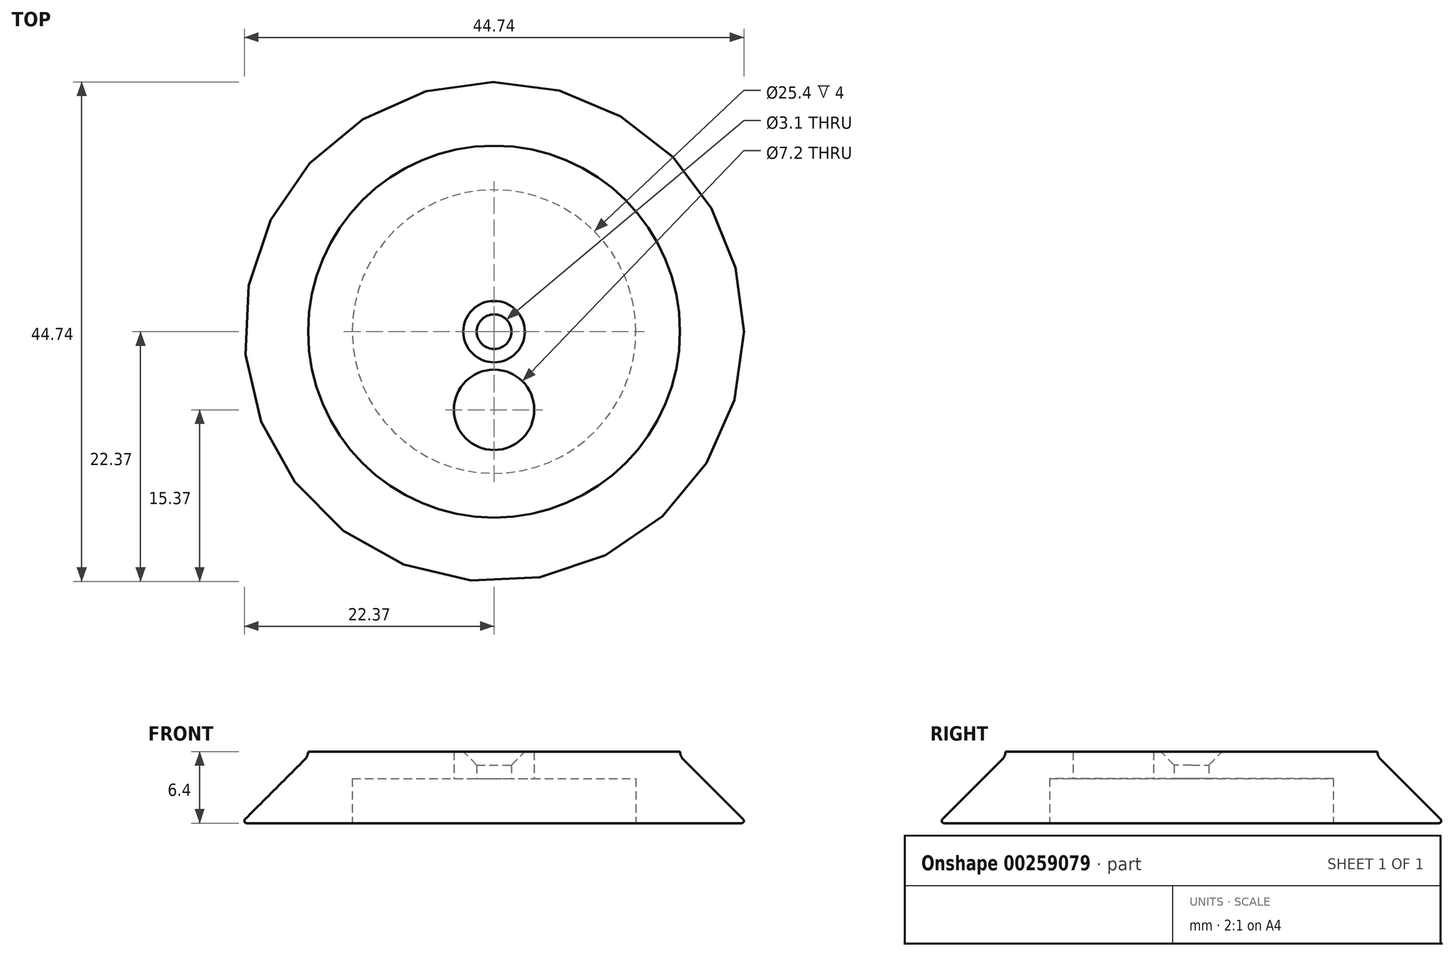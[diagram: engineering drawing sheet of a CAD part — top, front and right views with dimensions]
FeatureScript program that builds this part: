
annotation { "Feature Type Name" : "Feature", "Feature Type Description" : "" }
export const myFeature = defineFeature(function(context is Context, id is Id, definition is map)
    precondition{}
    {
        {
            var Q0;
            Q0=qCreatedBy(makeId("Top.planeOp"),FACE);
            var sketch = newSketch(context, id + "F0", { "sketchPlane" : qUnion([Q0])});
            skCircle(sketch, "E0", {"center": v(0, 0) * mm, "radius": 22.65 * mm});
            skSolve(sketch);
        }
        {
            var Q0;
            Q0 = qSketchRegion(id + "F0", true);
            extrude(context, id + "F1", {"entities" : qUnion([Q0]), "depth" : 6 * mm});
        }
        {
            var Q0;
            Q0=makeQuery(id+"F1.opExtrude","CAP_EDGE",EDGE,{"disambiguationData":[OSD([sQuery(id+"F0.wireOp",EDGE,"E0")])],"isStart":false});
            chamfer(context, id + "F2", {"entities" : qUnion([Q0]), "width" : 6 * mm, "tangentPropagation" : true});
        }
        {
            var Q0;
            Q0=makeQuery(id+"F1.opExtrude","CAP_FACE",FACE,{"disambiguationData":[OSD([sQuery(id+"F0.wireOp",EDGE,"E0")])],"isStart":false});
            extrude(context, id + "F3", {"entities" : qUnion([Q0]), "operationType" : NewBodyOperationType.ADD, "depth" : 0.4 * mm});
        }
        {
            var Q0;
            Q0=makeQuery(id+"F1.opExtrude","CAP_FACE",FACE,{"disambiguationData":[OSD([sQuery(id+"F0.wireOp",EDGE,"E0")])],"isStart":true});
            var sketch = newSketch(context, id + "F4", { "sketchPlane" : qUnion([Q0])});
            skCircle(sketch, "E1", {"center": v(0, 0) * mm, "radius": 12.7 * mm});
            skSolve(sketch);
        }
        {
            var Q0;
            Q0 = qSketchRegion(id + "F4", true);
            extrude(context, id + "F5", {"entities" : qUnion([Q0]), "operationType" : NewBodyOperationType.REMOVE, "oppositeDirection" : true, "depth" : 4 * mm});
        }
        {
            var Q0;
            {var subQ0=sQuery(id+"F0.wireOp",EDGE,"E0");Q0=makeQuery(id+"F2.opChamfer","BLEND_EDGE",EDGE,{"blendedFrom":[makeQuery(id+"F1.opExtrude","CAP_EDGE",EDGE,{"disambiguationData":[OSD([subQ0])],"isStart":false}),makeQuery(id+"F1.opExtrude","CAP_FACE",FACE,{"disambiguationData":[OSD([subQ0])],"isStart":true})],"blendedInto":[makeQuery(id+"F1.opExtrude","CAP_FACE",FACE,{"disambiguationData":[OSD([subQ0])],"isStart":true})]});}
            fillet(context, id + "F6", {"entities" : qUnion([Q0]), "radius" : 0.2 * mm, "tangentPropagation" : true, "allowEdgeOverflow" : false});
        }
        {
            var Q0;
            Q0=makeQuery(id+"F5.boolean.opBoolean","COPY",FACE,{"derivedFrom":makeQuery(id+"F5.opExtrude","CAP_FACE",FACE,{"disambiguationData":[OSD([sQuery(id+"F4.wireOp",EDGE,"E1")])],"isStart":false})});
            var sketch = newSketch(context, id + "F7", { "sketchPlane" : qUnion([Q0])});
            skCircle(sketch, "E2", {"center": v(0, 0) * mm, "radius": 1.55 * mm});
            skSolve(sketch);
        }
        {
            var Q0;
            Q0 = qSketchRegion(id + "F7", true);
            extrude(context, id + "F8", {"entities" : qUnion([Q0]), "operationType" : NewBodyOperationType.REMOVE, "oppositeDirection" : true, "depth" : 25 * mm});
        }
        {
            var Q0;
            Q0=makeQuery(id+"F5.boolean.opBoolean","COPY",FACE,{"derivedFrom":makeQuery(id+"F5.opExtrude","CAP_FACE",FACE,{"disambiguationData":[OSD([sQuery(id+"F4.wireOp",EDGE,"E1")])],"isStart":false})});
            var sketch = newSketch(context, id + "F9", { "sketchPlane" : qUnion([Q0])});
            skCircle(sketch, "E3", {"center": v(0, 7) * mm, "radius": 3.6 * mm});
            skSolve(sketch);
        }
        {
            var Q0;
            Q0 = qSketchRegion(id + "F9", true);
            extrude(context, id + "F10", {"entities" : qUnion([Q0]), "operationType" : NewBodyOperationType.REMOVE, "oppositeDirection" : true, "depth" : 25 * mm});
        }
        {
            var Q0;
            Q0=makeQuery(id+"F8.boolean.opBoolean","INTERSECT",EDGE,{"derivedFrom":[makeQuery(id+"F3.opExtrude","CAP_FACE",FACE,{"disambiguationData":[OSD([sQuery(id+"F0.wireOp",EDGE,"E0")])],"isStart":false}),makeQuery(id+"F8.opExtrude","SWEPT_FACE",FACE,{"disambiguationData":[OSD([sQuery(id+"F7.wireOp",EDGE,"E2")])]})]});
            chamfer(context, id + "F11", {"entities" : qUnion([Q0]), "width" : 1.2 * mm, "tangentPropagation" : true});
        }
        {
            var Q0;
            {var subQ0=sQuery(id+"F0.wireOp",EDGE,"E0");Q0=makeQuery(id+"F3.boolean.opBoolean","MERGE",EDGE,{"derivedFrom":[makeQuery(id+"F2.opChamfer","BLEND_EDGE",EDGE,{"blendedFrom":[makeQuery(id+"F1.opExtrude","CAP_EDGE",EDGE,{"disambiguationData":[OSD([subQ0])],"isStart":false}),makeQuery(id+"F1.opExtrude","CAP_FACE",FACE,{"disambiguationData":[OSD([subQ0])],"isStart":false})],"blendedInto":[makeQuery(id+"F1.opExtrude","CAP_FACE",FACE,{"disambiguationData":[OSD([subQ0])],"isStart":false})]}),makeQuery(id+"F3.opExtrude","CAP_EDGE",EDGE,{"disambiguationData":[OSD([subQ0])],"isStart":true})]});}
            fillet(context, id + "F12", {"entities" : qUnion([Q0]), "radius" : 1 * mm, "tangentPropagation" : true, "allowEdgeOverflow" : false});
        }
    });
